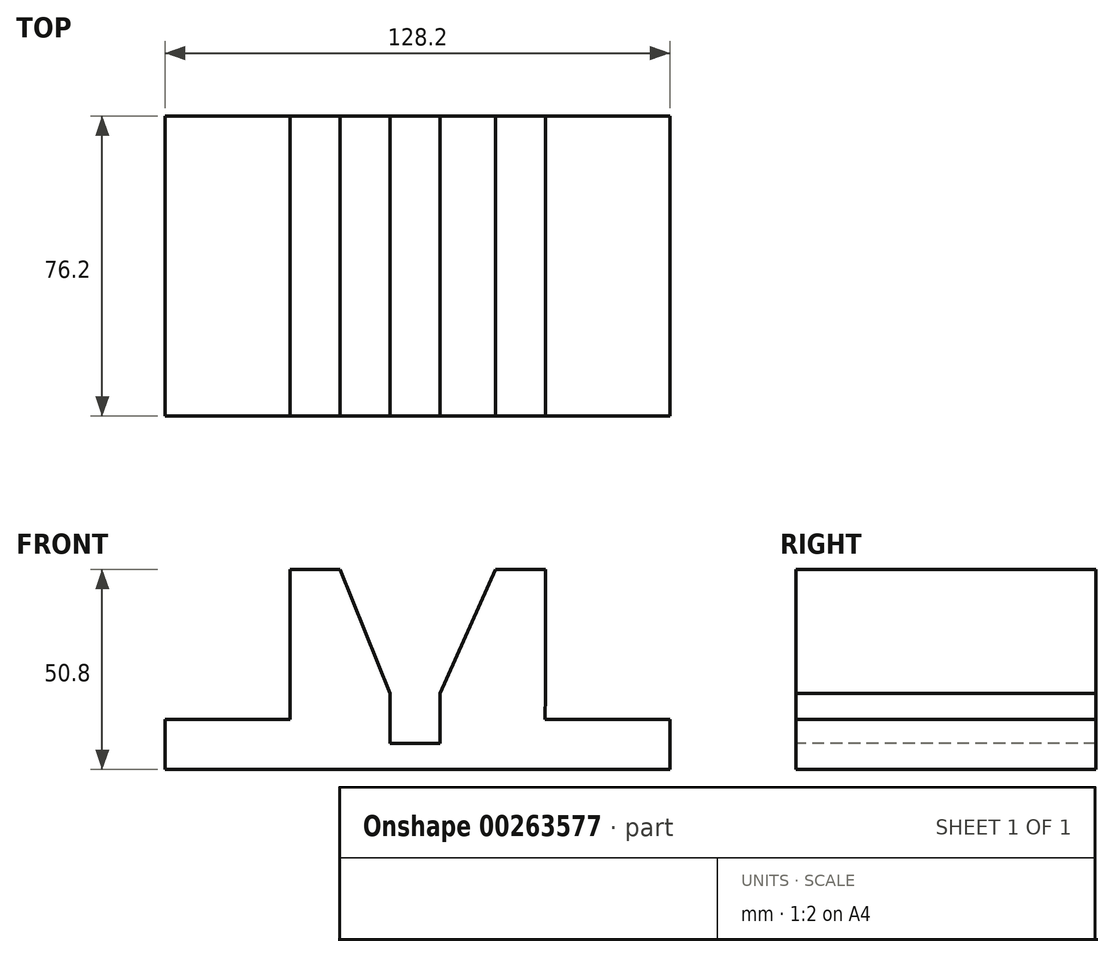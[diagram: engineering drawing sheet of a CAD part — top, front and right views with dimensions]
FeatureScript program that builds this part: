
annotation { "Feature Type Name" : "Feature", "Feature Type Description" : "" }
export const myFeature = defineFeature(function(context is Context, id is Id, definition is map)
    precondition{}
    {
        {
            var Q0;
            Q0=qCreatedBy(makeId("Front.planeOp"),FACE);
            var sketch = newSketch(context, id + "F0", { "sketchPlane" : qUnion([Q0])});
            skLineSegment(sketch, "E0.bottom", {"start": v(-75.84, 31.52) * mm, "end": v(76.56, 31.52) * mm});
            skLineSegment(sketch, "E0.top", {"start": v(-75.84, -19.28) * mm, "end": v(76.56, -19.28) * mm});
            skLineSegment(sketch, "E0.left", {"start": v(-75.84, 31.52) * mm, "end": v(-75.84, -19.28) * mm});
            skLineSegment(sketch, "E0.right", {"start": v(76.56, 31.52) * mm, "end": v(76.56, -19.28) * mm});
            skSolve(sketch);
        }
        {
            var Q0;
            Q0 = qSketchRegion(id + "F0", true);
            extrude(context, id + "F1", {"entities" : qUnion([Q0]), "depth" : 76.2 * mm});
        }
        {
            var Q0;
            Q0=makeQuery(id+"F1.opExtrude","CAP_FACE",FACE,{"disambiguationData":[OSD([sQuery(id+"F0.wireOp",EDGE,"E0.bottom"),sQuery(id+"F0.wireOp",EDGE,"E0.top"),sQuery(id+"F0.wireOp",EDGE,"E0.left"),sQuery(id+"F0.wireOp",EDGE,"E0.right")])],"isStart":false});
            var sketch = newSketch(context, id + "F2", { "sketchPlane" : qUnion([Q0])});
            skLineSegment(sketch, "E1", {"start": v(-75.84, -6.58) * mm, "end": v(-75.84, 31.52) * mm});
            skLineSegment(sketch, "E2", {"start": v(-75.84, 31.52) * mm, "end": v(-44.1, 31.52) * mm});
            skLineSegment(sketch, "E3", {"start": v(-44.1, 31.52) * mm, "end": v(-44.1, -6.58) * mm});
            skLineSegment(sketch, "E4", {"start": v(-44.1, -6.58) * mm, "end": v(-75.84, -6.58) * mm});
            skSolve(sketch);
        }
        {
            var Q0;
            Q0=makeQuery(id+"F2.imprint","IMPRINT",FACE,{"disambiguationData":[TD([[makeQuery(id+"F2.imprint","IMPRINT",EDGE,{"derivedFrom":sQuery(id+"F2.wireOp",EDGE,"E1")}),1.0]])]});
            extrude(context, id + "F3", {"entities" : qUnion([Q0]), "operationType" : NewBodyOperationType.REMOVE, "endBound" : BoundingType.THROUGH_ALL, "oppositeDirection" : true, "depth" : 25.4 * mm});
        }
        {
            var Q0;
            Q0=makeQuery(id+"F1.opExtrude","CAP_FACE",FACE,{"disambiguationData":[OSD([sQuery(id+"F0.wireOp",EDGE,"E0.bottom"),sQuery(id+"F0.wireOp",EDGE,"E0.top"),sQuery(id+"F0.wireOp",EDGE,"E0.left"),sQuery(id+"F0.wireOp",EDGE,"E0.right")])],"isStart":false});
            var sketch = newSketch(context, id + "F4", { "sketchPlane" : qUnion([Q0])});
            skLineSegment(sketch, "E5", {"start": v(-31.4, 31.52) * mm, "end": v(-18.7, 0) * mm});
            skLineSegment(sketch, "E6", {"start": v(-18.7, 0) * mm, "end": v(-18.7, -12.7) * mm});
            skLineSegment(sketch, "E7", {"start": v(-18.7, -12.7) * mm, "end": v(-6, -12.7) * mm});
            skLineSegment(sketch, "E8", {"start": v(-6, -12.7) * mm, "end": v(-6, 0) * mm});
            skLineSegment(sketch, "E9", {"start": v(-6, 0) * mm, "end": v(8.06, 31.52) * mm});
            skLineSegment(sketch, "E10", {"start": v(-31.4, 31.52) * mm, "end": v(8.06, 31.52) * mm});
            skPoint(sketch, "E11.end.orphan", {"position": v(-44.1, 0) * mm});
            skPoint(sketch, "E12.end.orphan", {"position": v(20.76, 0) * mm});
            skSolve(sketch);
        }
        {
            var Q0;
            Q0 = qSketchRegion(id + "F4", true);
            extrude(context, id + "F5", {"entities" : qUnion([Q0]), "operationType" : NewBodyOperationType.REMOVE, "endBound" : BoundingType.THROUGH_ALL, "oppositeDirection" : true, "depth" : 25.4 * mm});
        }
        {
            var Q0;
            Q0=makeQuery(id+"F1.opExtrude","CAP_FACE",FACE,{"disambiguationData":[OSD([sQuery(id+"F0.wireOp",EDGE,"E0.bottom"),sQuery(id+"F0.wireOp",EDGE,"E0.top"),sQuery(id+"F0.wireOp",EDGE,"E0.left"),sQuery(id+"F0.wireOp",EDGE,"E0.right")])],"isStart":false});
            var sketch = newSketch(context, id + "F6", { "sketchPlane" : qUnion([Q0])});
            skLineSegment(sketch, "E13", {"start": v(20.76, 31.52) * mm, "end": v(20.76, 0) * mm});
            skLineSegment(sketch, "E14", {"start": v(20.76, 0) * mm, "end": v(76.56, 0) * mm});
            skLineSegment(sketch, "E15", {"start": v(76.56, 0) * mm, "end": v(76.56, 31.52) * mm});
            skLineSegment(sketch, "E16", {"start": v(76.56, 31.52) * mm, "end": v(20.76, 31.52) * mm});
            skSolve(sketch);
        }
        {
            var Q0;
            Q0=makeQuery(id+"F6.imprint","IMPRINT",FACE,{"disambiguationData":[TD([[makeQuery(id+"F6.imprint","IMPRINT",EDGE,{"derivedFrom":sQuery(id+"F6.wireOp",EDGE,"E13")}),1.0]])]});
            extrude(context, id + "F7", {"entities" : qUnion([Q0]), "operationType" : NewBodyOperationType.REMOVE, "endBound" : BoundingType.THROUGH_ALL, "oppositeDirection" : true, "depth" : 25.4 * mm});
        }
        {
            var Q0;
            Q0=makeQuery(id+"F1.opExtrude","CAP_FACE",FACE,{"disambiguationData":[OSD([sQuery(id+"F0.wireOp",EDGE,"E0.bottom"),sQuery(id+"F0.wireOp",EDGE,"E0.top"),sQuery(id+"F0.wireOp",EDGE,"E0.left"),sQuery(id+"F0.wireOp",EDGE,"E0.right")])],"isStart":false});
            var sketch = newSketch(context, id + "F8", { "sketchPlane" : qUnion([Q0])});
            skLineSegment(sketch, "E17", {"start": v(20.61, -6.58) * mm, "end": v(20.76, 0) * mm});
            skLineSegment(sketch, "E18", {"start": v(20.76, 0) * mm, "end": v(20.7, -6.58) * mm});
            skLineSegment(sketch, "E19", {"start": v(20.61, -6.58) * mm, "end": v(76.56, -6.58) * mm});
            skLineSegment(sketch, "E20", {"start": v(76.56, -6.58) * mm, "end": v(76.56, 0) * mm});
            skLineSegment(sketch, "E21", {"start": v(76.56, 0) * mm, "end": v(20.76, 0) * mm});
            skPoint(sketch, "E22.orphan", {"position": v(20.61, -19.28) * mm});
            skSolve(sketch);
        }
        {
            var Q0;
            Q0 = qSketchRegion(id + "F8", true);
            extrude(context, id + "F9", {"entities" : qUnion([Q0]), "operationType" : NewBodyOperationType.REMOVE, "endBound" : BoundingType.THROUGH_ALL, "oppositeDirection" : true, "depth" : 25.4 * mm});
        }
        {
            var Q0;
            Q0=makeQuery(id+"F1.opExtrude","CAP_FACE",FACE,{"disambiguationData":[OSD([sQuery(id+"F0.wireOp",EDGE,"E0.bottom"),sQuery(id+"F0.wireOp",EDGE,"E0.top"),sQuery(id+"F0.wireOp",EDGE,"E0.left"),sQuery(id+"F0.wireOp",EDGE,"E0.right")])],"isStart":false});
            var sketch = newSketch(context, id + "F10", { "sketchPlane" : qUnion([Q0])});
            skLineSegment(sketch, "E23", {"start": v(52.36, -6.58) * mm, "end": v(52.36, -19.28) * mm});
            skLineSegment(sketch, "E24", {"start": v(52.36, -19.28) * mm, "end": v(76.56, -19.28) * mm});
            skLineSegment(sketch, "E25", {"start": v(76.56, -19.28) * mm, "end": v(76.56, -6.58) * mm});
            skLineSegment(sketch, "E26", {"start": v(76.56, -6.58) * mm, "end": v(52.36, -6.58) * mm});
            skSolve(sketch);
        }
        {
            var Q0;
            Q0 = qSketchRegion(id + "F10", true);
            extrude(context, id + "F11", {"entities" : qUnion([Q0]), "operationType" : NewBodyOperationType.REMOVE, "endBound" : BoundingType.THROUGH_ALL, "oppositeDirection" : true, "depth" : 25.4 * mm});
        }
    });
